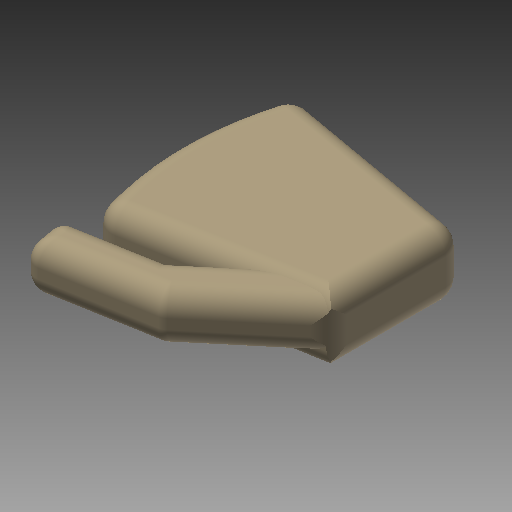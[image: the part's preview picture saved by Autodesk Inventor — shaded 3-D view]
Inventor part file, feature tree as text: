
AUTODESK INVENTOR PART (.ipt)
format: ipt  version: 2022 (Build 260153000, 153)  size: 322,048 bytes
history: native  units: mm (DEFAULTED — no unit token found)
features: fillet x4, other x3, extrude x3, plane x3, sketch x3, mirror x1
ambient origin geometry x8: Origin, YZ Plane, XZ Plane, XY Plane, X Axis, Y Axis, Z Axis, Center Point
bodies: Solid1 (feature_tree)
feature tree (17):
  other  "iMandy - 2D BODY"
  extrude  "Extrusion1"  Depth=10.0mm
  extrude  "Extrusion3"  Depth=54.0258mm
  mirror  "Mirror1"
  extrude  "Extrusion4"  Depth=27.0129mm
  fillet  "Fillet18"  [1 undecoded]
  fillet  "Fillet19"  [1 undecoded]
  fillet  "Fillet20"  Radius=1.350645mm
  fillet  "Fillet21"  [1 undecoded]
  plane  "Work Plane1"
  plane  "Work Plane2"
  other  "Work Axis1"
  plane  "Work Plane3"
  other  "Work Axis2"
  sketch  "Sketch1"  dims[d1=10.0mm d16=90.043mm]
  sketch  "Sketch3"  dims[d17=36.0172mm d18=54.0258mm]
  sketch  "Sketch4"  dims[d19=3.490659mm d20=27.0129mm d21=0.0mm d28=30.0deg d29=1.350645mm d30=0.0mm d35=0.0mm d40=78.787625mm d41=-4.051935mm d42=4.051935mm d43=4.051935mm d44=0.0mm d53=8.10387mm d54=5.40258mm d55=8.10387mm d56=13.50645mm]
note: 3 required parameter values undecoded (feature->parameter linkage not recoverable at this tier; creation-order binding heuristic only, values carry confidence <= 0.55)
